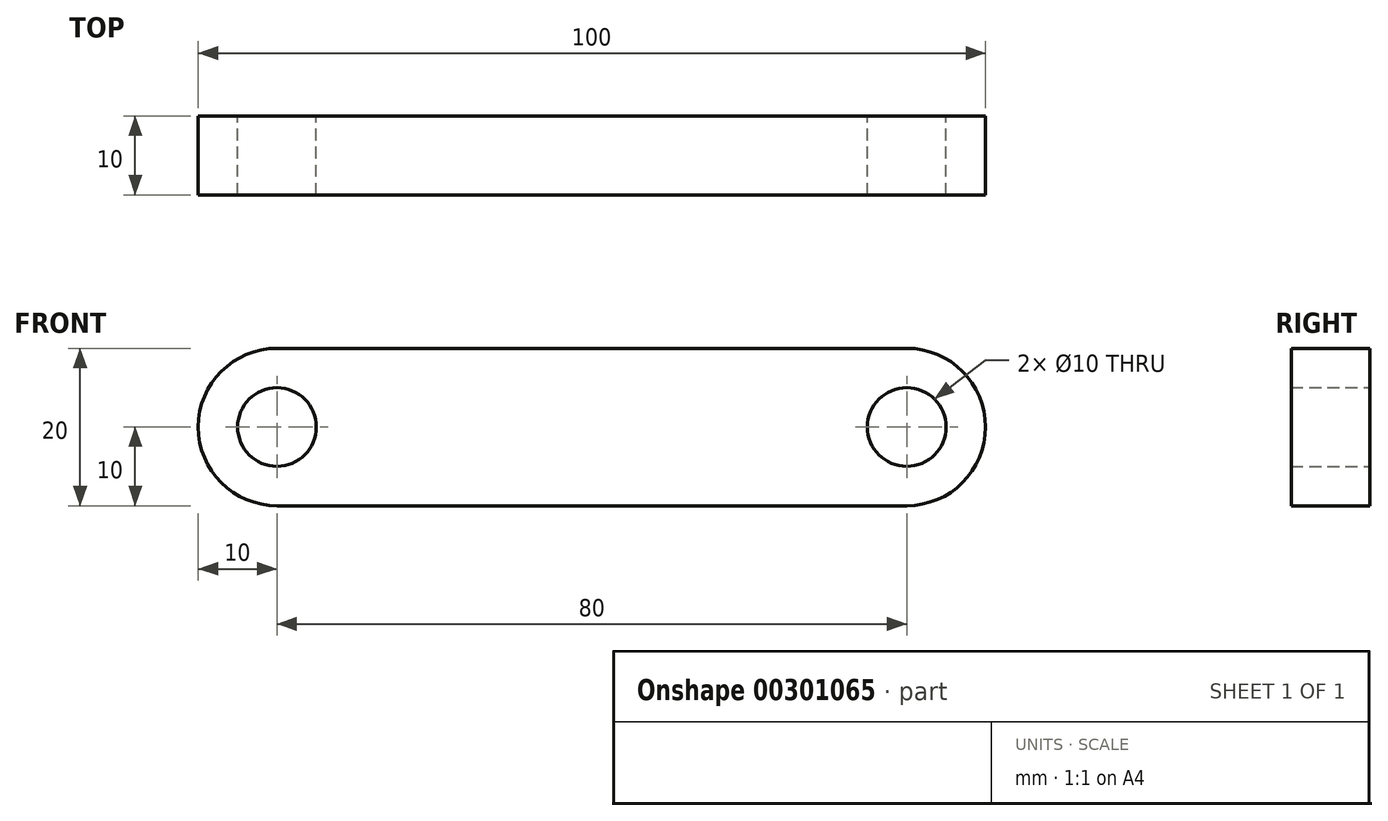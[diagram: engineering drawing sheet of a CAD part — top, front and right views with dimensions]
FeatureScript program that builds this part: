
annotation { "Feature Type Name" : "Feature", "Feature Type Description" : "" }
export const myFeature = defineFeature(function(context is Context, id is Id, definition is map)
    precondition{}
    {
        {
            var Q0;
            Q0=qCreatedBy(makeId("Front.planeOp"),FACE);
            var sketch = newSketch(context, id + "F0", { "sketchPlane" : qUnion([Q0])});
            skLineSegment(sketch, "E0.bottom", {"start": v(0, 0) * mm, "end": v(80, 0) * mm});
            skLineSegment(sketch, "E0.top", {"start": v(0, 20) * mm, "end": v(80, 20) * mm});
            skArc(sketch, "E1", {"start": v(0, 20) * mm, "mid": v(-10, 10) * mm, "end": v(0, 0) * mm});
            skArc(sketch, "E2", {"start": v(80, 20) * mm, "mid": v(90, 10) * mm, "end": v(80, 0) * mm});
            skCircle(sketch, "E3", {"center": v(0, 10) * mm, "radius": 5 * mm});
            skCircle(sketch, "E4", {"center": v(80, 10) * mm, "radius": 5 * mm});
            skSolve(sketch);
        }
        {
            var Q0;
            Q0 = qSketchRegion(id + "F0", true);
            extrude(context, id + "F1", {"entities" : qUnion([Q0]), "depth" : 10 * mm});
        }
    });
